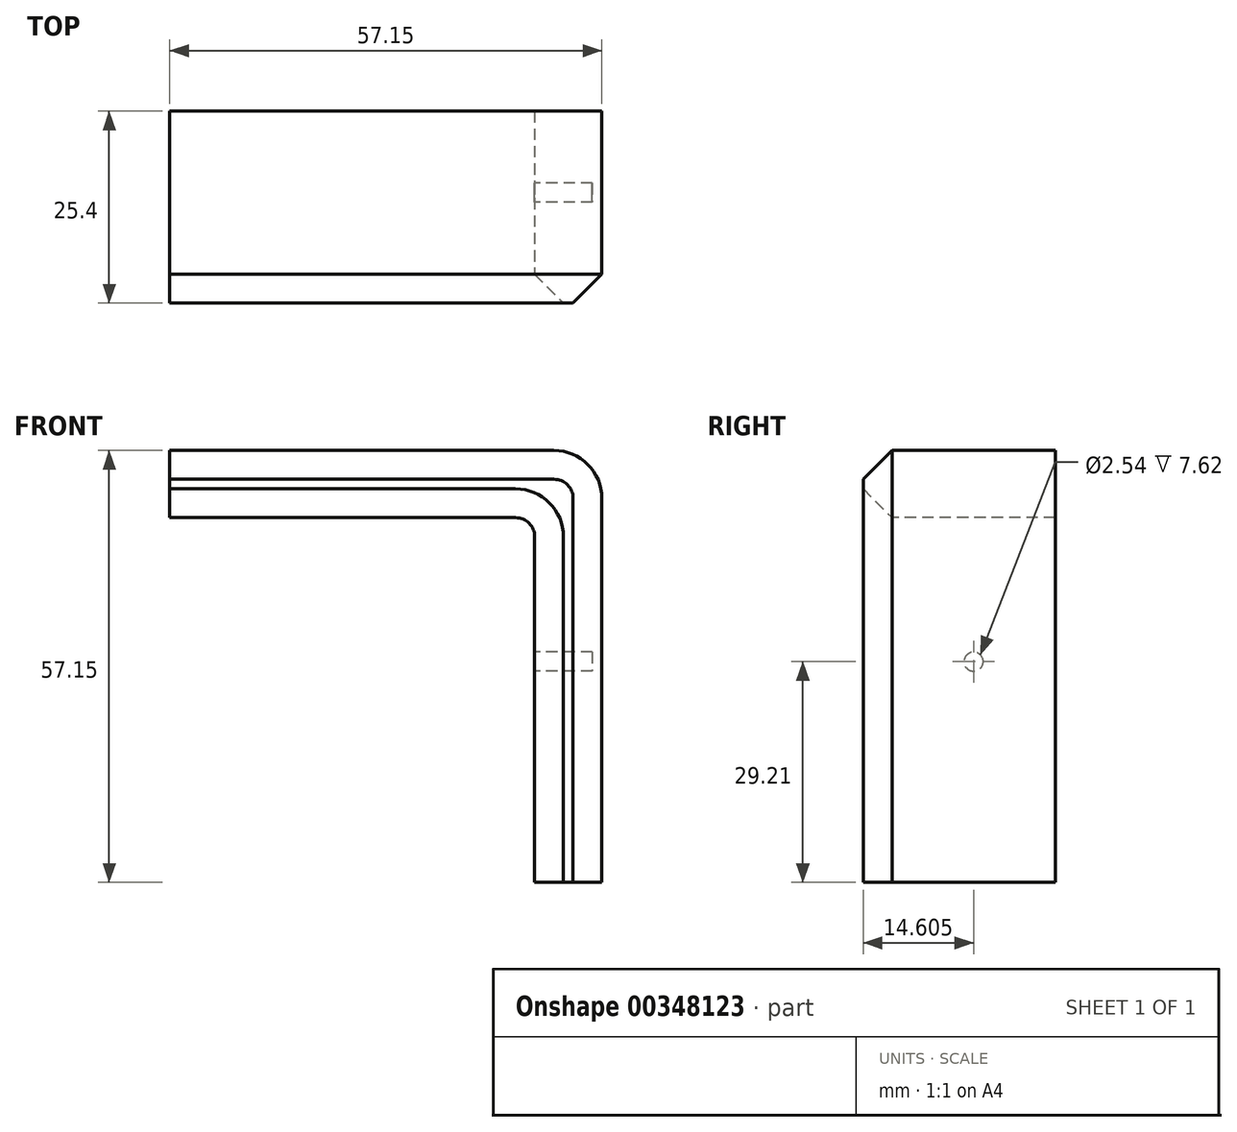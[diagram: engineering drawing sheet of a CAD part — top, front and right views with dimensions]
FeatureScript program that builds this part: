
annotation { "Feature Type Name" : "Feature", "Feature Type Description" : "" }
export const myFeature = defineFeature(function(context is Context, id is Id, definition is map)
    precondition{}
    {
        {
            var Q0;
            Q0=qCreatedBy(makeId("Front.planeOp"),FACE);
            var sketch = newSketch(context, id + "F0", { "sketchPlane" : qUnion([Q0])});
            skLineSegment(sketch, "E0", {"start": v(0, 25.4) * mm, "end": v(0, -25.4) * mm});
            skLineSegment(sketch, "E1", {"start": v(-6.35, 31.75) * mm, "end": v(-57.15, 31.75) * mm});
            skLineSegment(sketch, "E2", {"start": v(-57.15, 31.75) * mm, "end": v(-57.15, 22.86) * mm});
            skLineSegment(sketch, "E3", {"start": v(-57.15, 22.86) * mm, "end": v(-11.43, 22.86) * mm});
            skLineSegment(sketch, "E4", {"start": v(-8.9, 20.32) * mm, "end": v(-8.9, -25.4) * mm});
            skLineSegment(sketch, "E5", {"start": v(-8.9, -25.4) * mm, "end": v(0, -25.4) * mm});
            skPoint(sketch, "E6.visualSharp", {"position": v(-8.9, 22.86) * mm});
            skArc(sketch, "E6.filletArc", {"start": v(-8.9, 20.32) * mm, "mid": v(-9.63, 22.12) * mm, "end": v(-11.43, 22.86) * mm});
            skPoint(sketch, "E7.visualSharp", {"position": v(0, 31.75) * mm});
            skArc(sketch, "E7.filletArc", {"start": v(0, 25.4) * mm, "mid": v(-1.86, 29.9) * mm, "end": v(-6.35, 31.75) * mm});
            skSolve(sketch);
        }
        {
            var Q0;
            Q0=makeQuery(id+"F0.imprint","IMPRINT",FACE,{"disambiguationData":[TD([[makeQuery(id+"F0.imprint","IMPRINT",EDGE,{"derivedFrom":sQuery(id+"F0.wireOp",EDGE,"E0")}),-1.0]])]});
            extrude(context, id + "F1", {"entities" : qUnion([Q0]), "endBound" : BoundingType.SYMMETRIC, "oppositeDirection" : true, "depth" : 25.4 * mm});
        }
        {
            var Q0;
            Q0=makeQuery(id+"F1.opExtrude","CAP_EDGE",EDGE,{"disambiguationData":[OSD([sQuery(id+"F0.wireOp",EDGE,"E1")])],"isStart":true});
            var Q1;
            Q1=makeQuery(id+"F1.opExtrude","CAP_EDGE",EDGE,{"disambiguationData":[OSD([sQuery(id+"F0.wireOp",EDGE,"E3")])],"isStart":true});
            chamfer(context, id + "F2", {"entities" : qUnion([Q0, Q1]), "width" : 3.8 * mm, "tangentPropagation" : true});
        }
        {
            var Q0;
            Q0=makeQuery(id+"F1.opExtrude","SWEPT_FACE",FACE,{"disambiguationData":[OSD([sQuery(id+"F0.wireOp",EDGE,"E4")])]});
            var sketch = newSketch(context, id + "F3", { "sketchPlane" : qUnion([Q0])});
            skCircle(sketch, "E8", {"center": v(-1.9, 3.81) * mm, "radius": 1.27 * mm});
            skLineSegment(sketch, "E9", {"start": v(8.9, 3.81) * mm, "end": v(-12.7, 3.81) * mm, "construction": true});
            skSolve(sketch);
        }
        {
            var Q0;
            Q0=makeQuery(id+"F3.imprint","IMPRINT",FACE,{"disambiguationData":[TD([[makeQuery(id+"F3.imprint","IMPRINT",EDGE,{"derivedFrom":sQuery(id+"F3.wireOp",EDGE,"E8")}),1.0]])]});
            var Q1;
            Q1=makeQuery(id+"F1.opExtrude","SWEPT_FACE",FACE,{"disambiguationData":[OSD([sQuery(id+"F0.wireOp",EDGE,"E0")])]});
            extrude(context, id + "F4", {"entities" : qUnion([Q0]), "operationType" : NewBodyOperationType.REMOVE, "oppositeDirection" : true, "endBoundEntityFace" : qUnion([Q1]), "depth" : 7.62 * mm});
        }
    });
